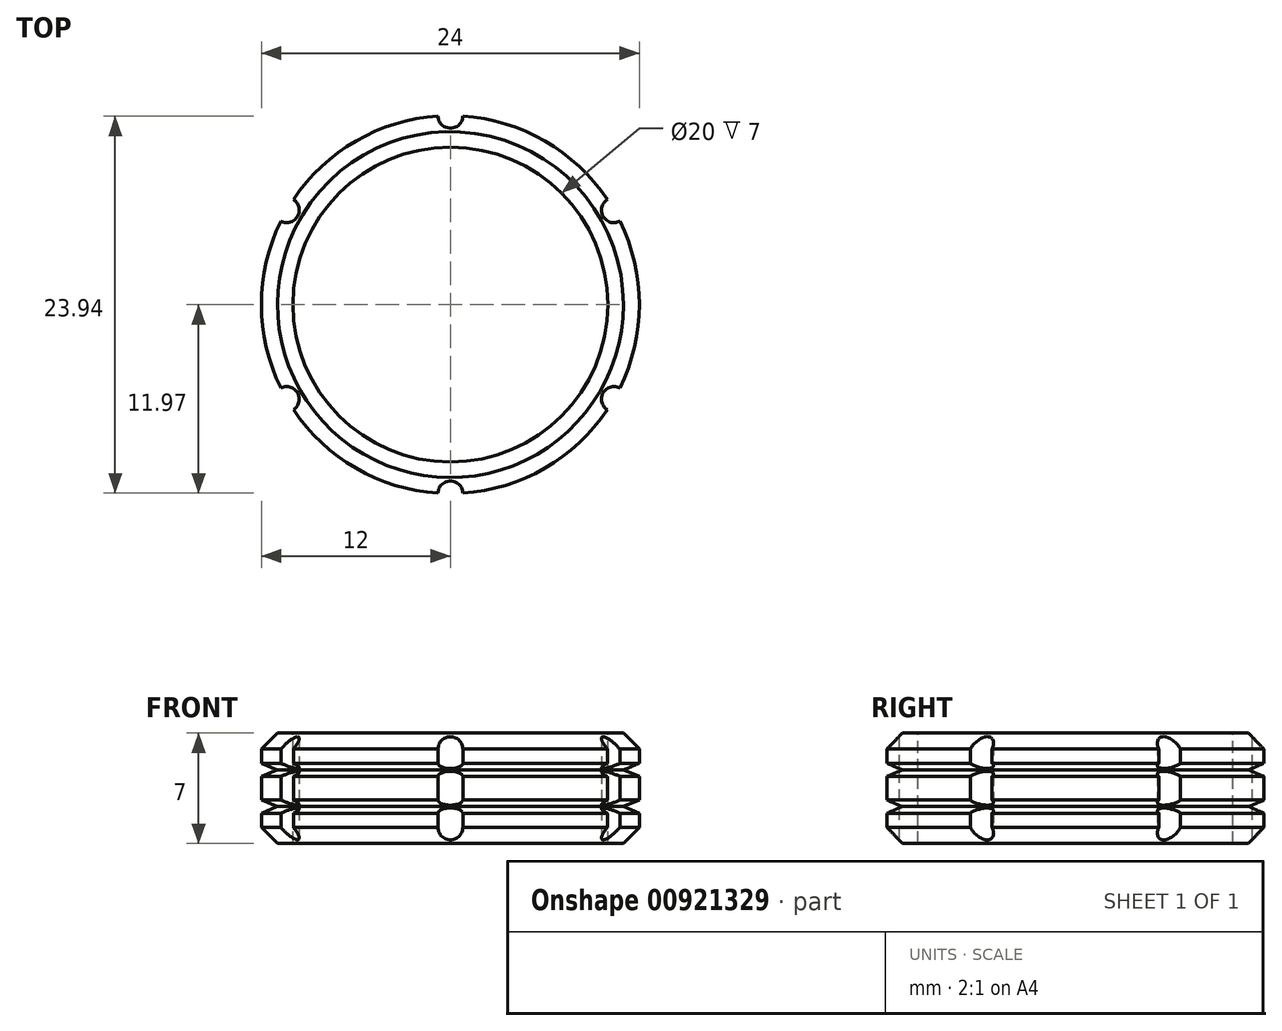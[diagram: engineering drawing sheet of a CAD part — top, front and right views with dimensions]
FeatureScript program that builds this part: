
annotation { "Feature Type Name" : "Feature", "Feature Type Description" : "" }
export const myFeature = defineFeature(function(context is Context, id is Id, definition is map)
    precondition{}
    {
        {
            var Q0;
            Q0=qCreatedBy(makeId("Front.planeOp"),FACE);
            var sketch = newSketch(context, id + "F0", { "sketchPlane" : qUnion([Q0])});
            skLineSegment(sketch, "E0", {"start": v(0, 11.46) * mm, "end": v(0, 0) * mm, "construction": true});
            skLineSegment(sketch, "E1", {"start": v(-10, 0) * mm, "end": v(-10, 7) * mm});
            skLineSegment(sketch, "E2", {"start": v(-10, 7) * mm, "end": v(-12, 7) * mm});
            skLineSegment(sketch, "E3", {"start": v(-12, 7) * mm, "end": v(-12, 5.09) * mm});
            skLineSegment(sketch, "E4", {"start": v(-12, 0) * mm, "end": v(-10, 0) * mm});
            skLineSegment(sketch, "E5", {"start": v(-12, 4.67) * mm, "end": v(-10, 4.67) * mm, "construction": true});
            skLineSegment(sketch, "E6", {"start": v(-12, 2.33) * mm, "end": v(-10, 2.33) * mm, "construction": true});
            skLineSegment(sketch, "E7", {"start": v(-12, 5.09) * mm, "end": v(-11, 4.67) * mm});
            skLineSegment(sketch, "E8", {"start": v(-11, 4.67) * mm, "end": v(-12, 4.25) * mm});
            skLineSegment(sketch, "E9", {"start": v(-11, 2.33) * mm, "end": v(-12, 2.75) * mm});
            skLineSegment(sketch, "E10", {"start": v(-11, 2.33) * mm, "end": v(-12, 1.91) * mm});
            skLineSegment(sketch, "E11.trimOffspring", {"start": v(-12, 1.91) * mm, "end": v(-12, 0) * mm});
            skLineSegment(sketch, "E12", {"start": v(-12, 4.25) * mm, "end": v(-12, 2.75) * mm});
            skSolve(sketch);
        }
        {
            var Q0;
            Q0=qSketchRegion(id+"F0",true);
            var Q1;
            Q1=sQuery(id+"F0.wireOp",EDGE,"E0");
            revolve(context, id + "F1", {"surfaceOperationType" : NewSurfaceOperationType.NEW, "entities" : qUnion([Q0]), "axis" : qUnion([Q1]), "revolveType" : RevolveType.FULL});
        }
        {
            var Q0;
            Q0=makeQuery(id+"F1.opRevolve","SWEPT_EDGE",EDGE,{"disambiguationData":[OSD([sQuery(id+"F0.wireOp",EDGE,"E2"),sQuery(id+"F0.wireOp",EDGE,"E3")])]});
            var Q1;
            Q1=makeQuery(id+"F1.opRevolve","SWEPT_EDGE",EDGE,{"disambiguationData":[OSD([sQuery(id+"F0.wireOp",EDGE,"E4"),sQuery(id+"F0.wireOp",EDGE,"E11.trimOffspring")])]});
            chamfer(context, id + "F2", {"entities" : qUnion([Q0, Q1]), "width" : 1.02 * mm, "tangentPropagation" : true});
        }
        {
            var Q0;
            Q0=qCreatedBy(makeId("Top.planeOp"),FACE);
            var sketch = newSketch(context, id + "F3", { "sketchPlane" : qUnion([Q0])});
            skCircle(sketch, "E13", {"center": v(0, -12) * mm, "radius": 0.8 * mm});
            skCircle(sketch, "E14.1.0", {"center": v(10.4, -6) * mm, "radius": 0.8 * mm});
            skCircle(sketch, "E14.2.0", {"center": v(10.4, 6) * mm, "radius": 0.8 * mm});
            skCircle(sketch, "E14.3.0", {"center": v(0, 12) * mm, "radius": 0.8 * mm});
            skCircle(sketch, "E14.4.0", {"center": v(-10.4, 6) * mm, "radius": 0.8 * mm});
            skCircle(sketch, "E14.5.0", {"center": v(-10.4, -6) * mm, "radius": 0.8 * mm});
            skPoint(sketch, "E14.center", {"position": v(0, 0) * mm});
            skSolve(sketch);
        }
        {
            var Q0;
            Q0=makeQuery(id+"F3.imprint","IMPRINT",FACE,{"disambiguationData":[TD([[makeQuery(id+"F3.imprint","IMPRINT",EDGE,{"derivedFrom":sQuery(id+"F3.wireOp",EDGE,"E14.5.0")}),1.0]])]});
            var Q1;
            Q1=makeQuery(id+"F3.imprint","IMPRINT",FACE,{"disambiguationData":[TD([[makeQuery(id+"F3.imprint","IMPRINT",EDGE,{"derivedFrom":sQuery(id+"F3.wireOp",EDGE,"E13")}),1.0]])]});
            var Q2;
            Q2=makeQuery(id+"F3.imprint","IMPRINT",FACE,{"disambiguationData":[TD([[makeQuery(id+"F3.imprint","IMPRINT",EDGE,{"derivedFrom":sQuery(id+"F3.wireOp",EDGE,"E14.1.0")}),1.0]])]});
            var Q3;
            Q3=makeQuery(id+"F3.imprint","IMPRINT",FACE,{"disambiguationData":[TD([[makeQuery(id+"F3.imprint","IMPRINT",EDGE,{"derivedFrom":sQuery(id+"F3.wireOp",EDGE,"E14.2.0")}),1.0]])]});
            var Q4;
            Q4=makeQuery(id+"F3.imprint","IMPRINT",FACE,{"disambiguationData":[TD([[makeQuery(id+"F3.imprint","IMPRINT",EDGE,{"derivedFrom":sQuery(id+"F3.wireOp",EDGE,"E14.3.0")}),1.0]])]});
            var Q5;
            Q5=makeQuery(id+"F3.imprint","IMPRINT",FACE,{"disambiguationData":[TD([[makeQuery(id+"F3.imprint","IMPRINT",EDGE,{"derivedFrom":sQuery(id+"F3.wireOp",EDGE,"E14.4.0")}),1.0]])]});
            extrude(context, id + "F4", {"entities" : qUnion([Q0, Q1, Q2, Q3, Q4, Q5]), "operationType" : NewBodyOperationType.REMOVE, "endBound" : BoundingType.THROUGH_ALL, "depth" : 25.4 * mm, "offsetDistance" : 25.4 * mm});
        }
    });
